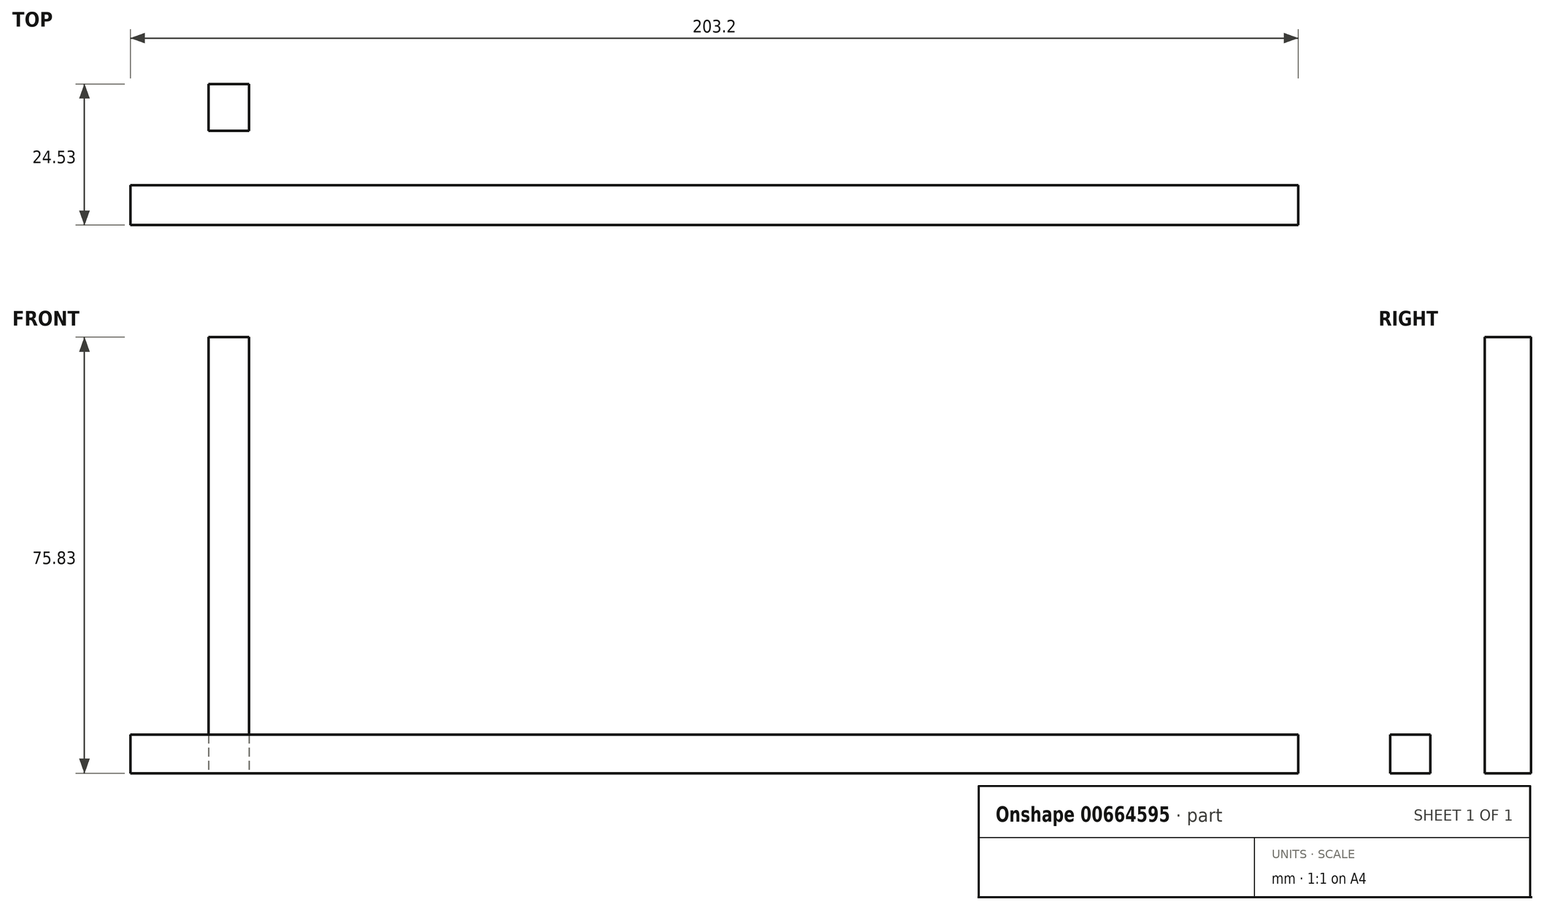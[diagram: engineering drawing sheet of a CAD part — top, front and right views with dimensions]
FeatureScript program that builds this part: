
annotation { "Feature Type Name" : "Feature", "Feature Type Description" : "" }
export const myFeature = defineFeature(function(context is Context, id is Id, definition is map)
    precondition{}
    {
        {
            var Q0;
            Q0=qCreatedBy(makeId("Right.planeOp"),FACE);
            var sketch = newSketch(context, id + "F0", { "sketchPlane" : qUnion([Q0])});
            skLineSegment(sketch, "E0.bottom", {"start": v(0, 0) * mm, "end": v(-6.96, 0) * mm});
            skLineSegment(sketch, "E0.top", {"start": v(0, 6.7) * mm, "end": v(-6.96, 6.7) * mm});
            skLineSegment(sketch, "E0.left", {"start": v(0, 0) * mm, "end": v(0, 6.7) * mm});
            skLineSegment(sketch, "E0.right", {"start": v(-6.96, 0) * mm, "end": v(-6.96, 6.7) * mm});
            skSolve(sketch);
        }
        {
            var Q0;
            Q0 = qSketchRegion(id + "F0", true);
            extrude(context, id + "F1", {"entities" : qUnion([Q0]), "oppositeDirection" : true, "depth" : 203.2 * mm, "offsetDistance" : 25.4 * mm});
        }
        {
            var Q0;
            Q0=qCreatedBy(makeId("Top.planeOp"),FACE);
            var sketch = newSketch(context, id + "F2", { "sketchPlane" : qUnion([Q0])});
            skLineSegment(sketch, "E1.bottom", {"start": v(-189.63, 9.46) * mm, "end": v(-182.58, 9.46) * mm});
            skLineSegment(sketch, "E1.top", {"start": v(-189.63, 17.57) * mm, "end": v(-182.58, 17.57) * mm});
            skLineSegment(sketch, "E1.left", {"start": v(-189.63, 9.46) * mm, "end": v(-189.63, 17.57) * mm});
            skLineSegment(sketch, "E1.right", {"start": v(-182.58, 9.46) * mm, "end": v(-182.58, 17.57) * mm});
            skSolve(sketch);
        }
        {
            var Q0;
            Q0 = qSketchRegion(id + "F2", true);
            extrude(context, id + "F3", {"entities" : qUnion([Q0]), "depth" : 75.83 * mm, "offsetDistance" : 25.4 * mm});
        }
    });
